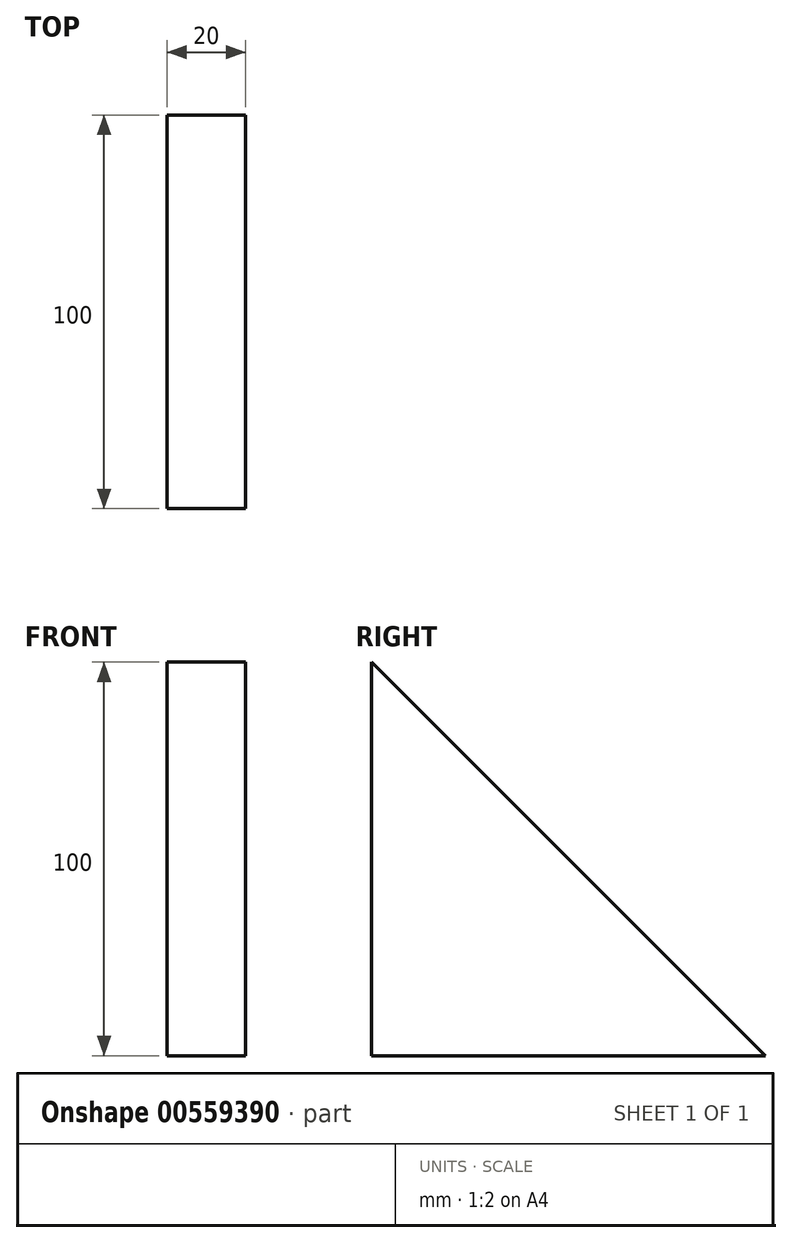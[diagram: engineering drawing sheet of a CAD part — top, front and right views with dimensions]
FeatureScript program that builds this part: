
annotation { "Feature Type Name" : "Feature", "Feature Type Description" : "" }
export const myFeature = defineFeature(function(context is Context, id is Id, definition is map)
    precondition{}
    {
        {
            var Q0;
            Q0=qCreatedBy(makeId("Right.planeOp"),FACE);
            var sketch = newSketch(context, id + "F0", { "sketchPlane" : qUnion([Q0])});
            skLineSegment(sketch, "E0", {"start": v(0, 0) * mm, "end": v(0, 100) * mm});
            skLineSegment(sketch, "E1", {"start": v(0, 0) * mm, "end": v(100, 0) * mm});
            skLineSegment(sketch, "E2", {"start": v(100, 0) * mm, "end": v(0, 100) * mm});
            skSolve(sketch);
        }
        {
            var Q0;
            Q0=makeQuery(id+"F0.imprint","IMPRINT",FACE,{"disambiguationData":[TD([[makeQuery(id+"F0.imprint","IMPRINT",EDGE,{"derivedFrom":sQuery(id+"F0.wireOp",EDGE,"E0")}),-1.0]])]});
            extrude(context, id + "F1", {"entities" : qUnion([Q0]), "depth" : 20 * mm, "offsetDistance" : 25 * mm});
        }
    });
